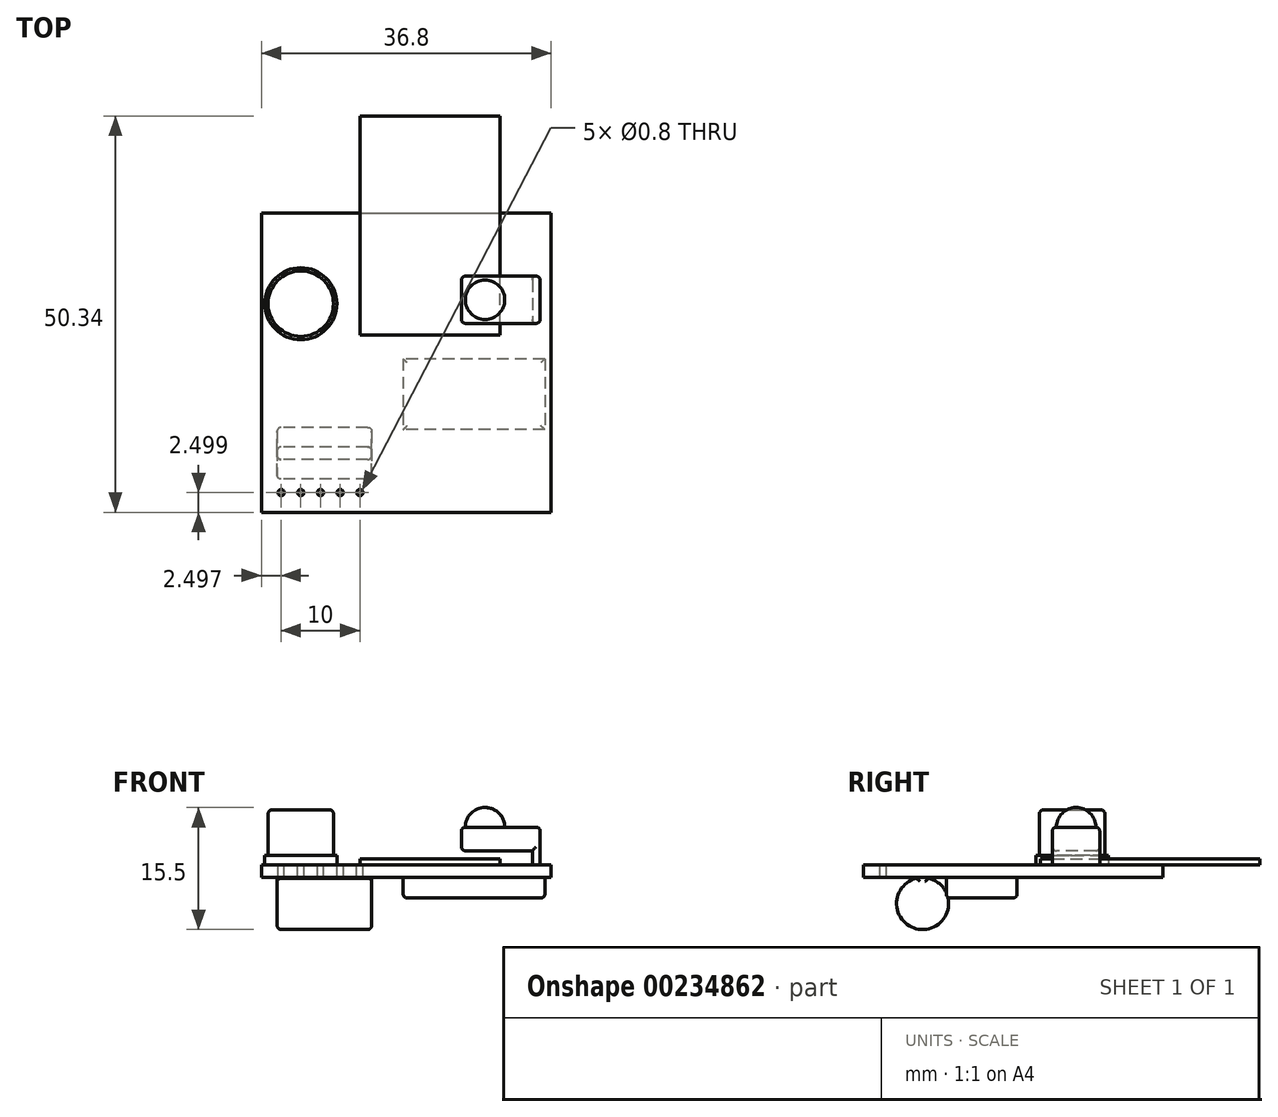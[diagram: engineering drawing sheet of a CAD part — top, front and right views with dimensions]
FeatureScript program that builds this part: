
annotation { "Feature Type Name" : "Feature", "Feature Type Description" : "" }
export const myFeature = defineFeature(function(context is Context, id is Id, definition is map)
    precondition{}
    {
        {
            var Q0;
            Q0=qCreatedBy(makeId("Top.planeOp"),FACE);
            var sketch = newSketch(context, id + "F0", { "sketchPlane" : qUnion([Q0])});
            skCircle(sketch, "E0", {"center": v(-33.02, 18.3) * mm, "radius": 4.15 * mm});
            skLineSegment(sketch, "E1.bottom", {"start": v(-38.02, 29.8) * mm, "end": v(-1.22, 29.8) * mm});
            skLineSegment(sketch, "E1.top", {"start": v(-38.02, -8.2) * mm, "end": v(-1.22, -8.2) * mm});
            skLineSegment(sketch, "E1.left", {"start": v(-38.02, 29.8) * mm, "end": v(-38.02, -8.2) * mm});
            skLineSegment(sketch, "E1.right", {"start": v(-1.22, 29.8) * mm, "end": v(-1.22, -8.2) * mm});
            skLineSegment(sketch, "E2", {"start": v(-33.02, 18.3) * mm, "end": v(-38.02, 18.3) * mm, "construction": true});
            skLineSegment(sketch, "E3", {"start": v(-33.02, 18.3) * mm, "end": v(-33.02, 29.8) * mm, "construction": true});
            skLineSegment(sketch, "E4", {"start": v(-7.72, 29.8) * mm, "end": v(-7.72, 42.15) * mm});
            skLineSegment(sketch, "E5", {"start": v(-7.72, 42.15) * mm, "end": v(-25.52, 42.15) * mm});
            skLineSegment(sketch, "E6", {"start": v(-25.52, 42.15) * mm, "end": v(-25.52, 29.8) * mm});
            skLineSegment(sketch, "E7", {"start": v(-2.62, 21.8) * mm, "end": v(-12.62, 21.8) * mm});
            skLineSegment(sketch, "E8", {"start": v(-12.62, 21.8) * mm, "end": v(-12.62, 15.8) * mm});
            skLineSegment(sketch, "E9", {"start": v(-12.62, 15.8) * mm, "end": v(-2.62, 15.8) * mm});
            skLineSegment(sketch, "E10", {"start": v(-2.62, 15.8) * mm, "end": v(-2.62, 21.8) * mm});
            skSolve(sketch);
        }
        {
            var Q0;
            Q0=makeQuery(id+"F0.imprint","IMPRINT",FACE,{"disambiguationData":[TD([[makeQuery(id+"F0.imprint","IMPRINT",EDGE,{"derivedFrom":sQuery(id+"F0.wireOp",EDGE,"E0")}),-1.0]])]});
            var Q1;
            Q1=makeQuery(id+"F0.imprint","IMPRINT",FACE,{"disambiguationData":[TD([[makeQuery(id+"F0.imprint","IMPRINT",EDGE,{"derivedFrom":sQuery(id+"F0.wireOp",EDGE,"E0")}),1.0]])]});
            var Q2;
            Q2=makeQuery(id+"F0.imprint","IMPRINT",FACE,{"disambiguationData":[TD([[makeQuery(id+"F0.imprint","IMPRINT",EDGE,{"derivedFrom":sQuery(id+"F0.wireOp",EDGE,"E7")}),1.0]])]});
            extrude(context, id + "F1", {"entities" : qUnion([Q0, Q1, Q2]), "oppositeDirection" : true, "depth" : 1.6 * mm});
        }
        {
            var Q0;
            Q0=makeQuery(id+"F0.imprint","IMPRINT",FACE,{"disambiguationData":[TD([[makeQuery(id+"F0.imprint","IMPRINT",EDGE,{"derivedFrom":sQuery(id+"F0.wireOp",EDGE,"E0")}),-1.0]])]});
            var sketch = newSketch(context, id + "F2", { "sketchPlane" : qUnion([Q0])});
            skCircle(sketch, "E11.0", {"center": v(-33.02, 18.3) * mm, "radius": 4.15 * mm});
            skLineSegment(sketch, "E12.0.0", {"start": v(-12.62, 15.8) * mm, "end": v(-2.62, 15.8) * mm});
            skLineSegment(sketch, "E12.0.1", {"start": v(-2.62, 15.8) * mm, "end": v(-2.62, 21.8) * mm});
            skLineSegment(sketch, "E12.0.2", {"start": v(-2.62, 21.8) * mm, "end": v(-12.62, 21.8) * mm});
            skLineSegment(sketch, "E12.0.3", {"start": v(-12.62, 21.8) * mm, "end": v(-12.62, 15.8) * mm});
            skLineSegment(sketch, "E13.0.0", {"start": v(-7.72, 42.15) * mm, "end": v(-25.52, 42.15) * mm});
            skLineSegment(sketch, "E13.0.1", {"start": v(-25.52, 42.15) * mm, "end": v(-25.52, 29.8) * mm});
            skLineSegment(sketch, "E13.0.2", {"start": v(-25.52, 29.8) * mm, "end": v(-7.72, 29.8) * mm});
            skLineSegment(sketch, "E13.0.3", {"start": v(-7.72, 29.8) * mm, "end": v(-7.72, 42.15) * mm});
            skLineSegment(sketch, "E14", {"start": v(-25.52, 29.8) * mm, "end": v(-25.52, 14.3) * mm});
            skLineSegment(sketch, "E15", {"start": v(-25.52, 14.3) * mm, "end": v(-7.72, 14.3) * mm});
            skLineSegment(sketch, "E16", {"start": v(-7.72, 14.3) * mm, "end": v(-7.72, 29.8) * mm});
            skCircle(sketch, "E17", {"center": v(-33.02, 18.3) * mm, "radius": 4.58 * mm});
            skSolve(sketch);
        }
        {
            var Q0;
            Q0=makeQuery(id+"F2.imprint","IMPRINT",FACE,{"disambiguationData":[TD([[makeQuery(id+"F2.imprint","IMPRINT",EDGE,{"derivedFrom":sQuery(id+"F2.wireOp",EDGE,"E11.0")}),-1.0]])]});
            var Q1;
            Q1=makeQuery(id+"F2.imprint","IMPRINT",FACE,{"disambiguationData":[TD([[makeQuery(id+"F2.imprint","IMPRINT",EDGE,{"derivedFrom":sQuery(id+"F2.wireOp",EDGE,"E11.0")}),1.0]])]});
            extrude(context, id + "F3", {"entities" : qUnion([Q0, Q1]), "operationType" : NewBodyOperationType.ADD, "depth" : 1.2 * mm});
        }
        {
            var Q0;
            Q0=makeQuery(id+"F3.opExtrude","CAP_FACE",FACE,{"disambiguationData":[OSD([sQuery(id+"F2.wireOp",EDGE,"E17")])],"isStart":false});
            var sketch = newSketch(context, id + "F4", { "sketchPlane" : qUnion([Q0])});
            skCircle(sketch, "E18.0", {"center": v(-33.02, 18.3) * mm, "radius": 4.15 * mm});
            skSolve(sketch);
        }
        {
            var Q0;
            Q0=makeQuery(id+"F4.imprint","IMPRINT",FACE,{"disambiguationData":[TD([[makeQuery(id+"F4.imprint","IMPRINT",EDGE,{"derivedFrom":sQuery(id+"F4.wireOp",EDGE,"E18.0")}),1.0]])]});
            extrude(context, id + "F5", {"entities" : qUnion([Q0]), "operationType" : NewBodyOperationType.ADD, "depth" : 5.8 * mm});
        }
        {
            var Q0;
            {var subQ0=sQuery(id+"F2.wireOp",EDGE,"E12.0.3");Q0=makeQuery(id+"F2.imprint","IMPRINT",FACE,{"disambiguationData":[TD([[makeQuery(id+"F2.imprint","IMPRINT",EDGE,{"derivedFrom":subQ0}),1.0]])]});}
            var Q1;
            {var subQ0=sQuery(id+"F2.wireOp",EDGE,"E12.0.3");Q1=makeQuery(id+"F2.imprint","IMPRINT",FACE,{"disambiguationData":[TD([[makeQuery(id+"F2.imprint","IMPRINT",EDGE,{"derivedFrom":subQ0}),-1.0]])]});}
            var Q2;
            Q2=makeQuery(id+"F2.imprint","IMPRINT",FACE,{"disambiguationData":[TD([[makeQuery(id+"F2.imprint","IMPRINT",EDGE,{"derivedFrom":sQuery(id+"F2.wireOp",EDGE,"E13.0.0")}),1.0]])]});
            extrude(context, id + "F6", {"entities" : qUnion([Q0, Q1, Q2]), "operationType" : NewBodyOperationType.ADD, "depth" : 0.8 * mm});
        }
        {
            var Q0;
            Q0=makeQuery(id+"F6.opExtrude","CAP_FACE",FACE,{"disambiguationData":[OSD([sQuery(id+"F2.wireOp",EDGE,"E13.0.0"),sQuery(id+"F2.wireOp",EDGE,"E13.0.1"),sQuery(id+"F2.wireOp",EDGE,"E13.0.3"),sQuery(id+"F2.wireOp",EDGE,"E14"),sQuery(id+"F2.wireOp",EDGE,"E15"),sQuery(id+"F2.wireOp",EDGE,"E16")])],"isStart":false});
            cPlane(context, id + "F7", {"entities" : qUnion([Q0]), "cplaneType" : CPlaneType.OFFSET, "offset" : 1 * mm, "width" : 150 * mm, "height" : 150 * mm});
        }
        {
            var Q0;
            Q0=qCreatedBy(id+"F7.planeOp",FACE);
            var sketch = newSketch(context, id + "F8", { "sketchPlane" : qUnion([Q0])});
            skLineSegment(sketch, "E19.0", {"start": v(-2.62, 21.8) * mm, "end": v(-12.62, 21.8) * mm});
            skLineSegment(sketch, "E20.0", {"start": v(-2.62, 15.8) * mm, "end": v(-2.62, 21.8) * mm});
            skLineSegment(sketch, "E21.0", {"start": v(-12.62, 15.8) * mm, "end": v(-2.62, 15.8) * mm});
            skLineSegment(sketch, "E22.0", {"start": v(-12.62, 21.8) * mm, "end": v(-12.62, 15.8) * mm});
            skSolve(sketch);
        }
        {
            var Q0;
            {var subQ10=sQuery(id+"F2.wireOp",EDGE,"E12.0.1");Q0=makeQuery(id+"F2.imprint","IMPRINT",FACE,{"disambiguationData":[TD([[makeQuery(id+"F2.imprint","IMPRINT",EDGE,{"derivedFrom":subQ10}),-1.0]])]});}
            var sketch = newSketch(context, id + "F9", { "sketchPlane" : qUnion([Q0])});
            skLineSegment(sketch, "E23", {"start": v(-3.62, 21.8) * mm, "end": v(-3.62, 15.8) * mm});
            skLineSegment(sketch, "E24", {"start": v(-3.62, 15.8) * mm, "end": v(-2.62, 15.8) * mm});
            skLineSegment(sketch, "E25", {"start": v(-2.62, 15.8) * mm, "end": v(-2.62, 21.8) * mm});
            skLineSegment(sketch, "E26", {"start": v(-2.62, 21.8) * mm, "end": v(-3.62, 21.8) * mm});
            skSolve(sketch);
        }
        {
            var Q0;
            Q0=makeQuery(id+"F9.imprint","IMPRINT",FACE,{"disambiguationData":[TD([[makeQuery(id+"F9.imprint","IMPRINT",EDGE,{"derivedFrom":sQuery(id+"F9.wireOp",EDGE,"E23")}),1.0]])]});
            extrude(context, id + "F10", {"entities" : qUnion([Q0]), "operationType" : NewBodyOperationType.ADD, "depth" : 1.8 * mm});
        }
        {
            var Q0;
            Q0=makeQuery(id+"F8.imprint","IMPRINT",FACE,{"disambiguationData":[TD([[makeQuery(id+"F8.imprint","IMPRINT",EDGE,{"derivedFrom":sQuery(id+"F8.wireOp",EDGE,"E19.0")}),1.0]])]});
            extrude(context, id + "F11", {"entities" : qUnion([Q0]), "operationType" : NewBodyOperationType.ADD, "depth" : 3 * mm});
        }
        {
            var Q0;
            Q0=makeQuery(id+"F11.opExtrude","CAP_FACE",FACE,{"disambiguationData":[OSD([sQuery(id+"F8.wireOp",EDGE,"E19.0"),sQuery(id+"F8.wireOp",EDGE,"E20.0"),sQuery(id+"F8.wireOp",EDGE,"E21.0"),sQuery(id+"F8.wireOp",EDGE,"E22.0")])],"isStart":false});
            var sketch = newSketch(context, id + "F12", { "sketchPlane" : qUnion([Q0])});
            skCircle(sketch, "E27", {"center": v(-9.62, 18.8) * mm, "radius": 2.5 * mm});
            skSolve(sketch);
        }
        {
            var Q0;
            Q0=makeQuery(id+"F12.imprint","IMPRINT",FACE,{"disambiguationData":[TD([[makeQuery(id+"F12.imprint","IMPRINT",EDGE,{"derivedFrom":sQuery(id+"F12.wireOp",EDGE,"E27")}),1.0]])]});
            extrude(context, id + "F13", {"entities" : qUnion([Q0]), "operationType" : NewBodyOperationType.ADD, "depth" : 2.5 * mm});
        }
        {
            var Q0;
            Q0=makeQuery(id+"F13.opExtrude","CAP_EDGE",EDGE,{"disambiguationData":[OSD([sQuery(id+"F12.wireOp",EDGE,"E27")])],"isStart":false});
            fillet(context, id + "F14", {"entities" : qUnion([Q0]), "radius" : 2.5 * mm, "tangentPropagation" : true, "allowEdgeOverflow" : false});
        }
        {
            var Q0;
            Q0=makeQuery(id+"F11.opExtrude","CAP_EDGE",EDGE,{"disambiguationData":[OSD([sQuery(id+"F8.wireOp",EDGE,"E21.0")])],"isStart":false});
            var Q1;
            Q1=makeQuery(id+"F11.opExtrude","CAP_EDGE",EDGE,{"disambiguationData":[OSD([sQuery(id+"F8.wireOp",EDGE,"E19.0")])],"isStart":false});
            var Q2;
            Q2=makeQuery(id+"F11.opExtrude","CAP_EDGE",EDGE,{"disambiguationData":[OSD([sQuery(id+"F8.wireOp",EDGE,"E20.0")])],"isStart":false});
            var Q3;
            Q3=makeQuery(id+"F11.boolean.opBoolean","MERGE",EDGE,{"derivedFrom":[makeQuery(id+"F10.opExtrude","SWEPT_EDGE",EDGE,{"disambiguationData":[OSD([sQuery(id+"F9.wireOp",EDGE,"E24"),sQuery(id+"F9.wireOp",EDGE,"E25")])]}),makeQuery(id+"F11.opExtrude","SWEPT_EDGE",EDGE,{"disambiguationData":[OSD([sQuery(id+"F8.wireOp",EDGE,"E20.0"),sQuery(id+"F8.wireOp",EDGE,"E21.0")])]})]});
            var Q4;
            Q4=makeQuery(id+"F11.boolean.opBoolean","MERGE",EDGE,{"derivedFrom":[makeQuery(id+"F10.opExtrude","SWEPT_EDGE",EDGE,{"disambiguationData":[OSD([sQuery(id+"F9.wireOp",EDGE,"E25"),sQuery(id+"F9.wireOp",EDGE,"E26")])]}),makeQuery(id+"F11.opExtrude","SWEPT_EDGE",EDGE,{"disambiguationData":[OSD([sQuery(id+"F8.wireOp",EDGE,"E19.0"),sQuery(id+"F8.wireOp",EDGE,"E20.0")])]})]});
            var Q5;
            Q5=makeQuery(id+"F10.opExtrude","SWEPT_EDGE",EDGE,{"disambiguationData":[OSD([sQuery(id+"F2.wireOp",EDGE,"E12.0.0"),sQuery(id+"F9.wireOp",EDGE,"E23"),sQuery(id+"F9.wireOp",EDGE,"E24")])]});
            var Q6;
            Q6=makeQuery(id+"F11.opExtrude","CAP_EDGE",EDGE,{"disambiguationData":[OSD([sQuery(id+"F8.wireOp",EDGE,"E21.0")])],"isStart":true});
            var Q7;
            Q7=makeQuery(id+"F11.opExtrude","SWEPT_FACE",FACE,{"disambiguationData":[OSD([sQuery(id+"F8.wireOp",EDGE,"E22.0")])]});
            var Q8;
            Q8=makeQuery(id+"F11.opExtrude","CAP_EDGE",EDGE,{"disambiguationData":[OSD([sQuery(id+"F8.wireOp",EDGE,"E19.0")])],"isStart":true});
            var Q9;
            Q9=makeQuery(id+"F10.opExtrude","SWEPT_EDGE",EDGE,{"disambiguationData":[OSD([sQuery(id+"F2.wireOp",EDGE,"E12.0.2"),sQuery(id+"F9.wireOp",EDGE,"E23"),sQuery(id+"F9.wireOp",EDGE,"E26")])]});
            var Q10;
            Q10=makeQuery(id+"F5.opExtrude","CAP_FACE",FACE,{"disambiguationData":[OSD([sQuery(id+"F4.wireOp",EDGE,"E18.0")])],"isStart":false});
            fillet(context, id + "F15", {"entities" : qUnion([Q0, Q1, Q2, Q3, Q4, Q5, Q6, Q7, Q8, Q9, Q10]), "radius" : 0.5 * mm, "tangentPropagation" : true, "allowEdgeOverflow" : false});
        }
        {
            var Q0;
            Q0=makeQuery(id+"F1.opExtrude","CAP_FACE",FACE,{"disambiguationData":[OSD([sQuery(id+"F0.wireOp",EDGE,"E1.bottom"),sQuery(id+"F0.wireOp",EDGE,"E1.top"),sQuery(id+"F0.wireOp",EDGE,"E1.left"),sQuery(id+"F0.wireOp",EDGE,"E1.right")])],"isStart":true});
            var sketch = newSketch(context, id + "F16", { "sketchPlane" : qUnion([Q0])});
            skCircle(sketch, "E28", {"center": v(-35.52, -5.7) * mm, "radius": 0.4 * mm});
            skCircle(sketch, "E29", {"center": v(-33.02, -5.7) * mm, "radius": 0.4 * mm});
            skCircle(sketch, "E30", {"center": v(-30.52, -5.7) * mm, "radius": 0.4 * mm});
            skCircle(sketch, "E31", {"center": v(-28.02, -5.7) * mm, "radius": 0.4 * mm});
            skCircle(sketch, "E32", {"center": v(-25.52, -5.7) * mm, "radius": 0.4 * mm});
            skSolve(sketch);
        }
        {
            var Q0;
            Q0=makeQuery(id+"F16.imprint","IMPRINT",FACE,{"disambiguationData":[TD([[makeQuery(id+"F16.imprint","IMPRINT",EDGE,{"derivedFrom":sQuery(id+"F16.wireOp",EDGE,"E28")}),1.0]])]});
            var Q1;
            Q1=makeQuery(id+"F16.imprint","IMPRINT",FACE,{"disambiguationData":[TD([[makeQuery(id+"F16.imprint","IMPRINT",EDGE,{"derivedFrom":sQuery(id+"F16.wireOp",EDGE,"E29")}),1.0]])]});
            var Q2;
            Q2=makeQuery(id+"F16.imprint","IMPRINT",FACE,{"disambiguationData":[TD([[makeQuery(id+"F16.imprint","IMPRINT",EDGE,{"derivedFrom":sQuery(id+"F16.wireOp",EDGE,"E30")}),1.0]])]});
            var Q3;
            Q3=makeQuery(id+"F16.imprint","IMPRINT",FACE,{"disambiguationData":[TD([[makeQuery(id+"F16.imprint","IMPRINT",EDGE,{"derivedFrom":sQuery(id+"F16.wireOp",EDGE,"E31")}),1.0]])]});
            var Q4;
            Q4=makeQuery(id+"F16.imprint","IMPRINT",FACE,{"disambiguationData":[TD([[makeQuery(id+"F16.imprint","IMPRINT",EDGE,{"derivedFrom":sQuery(id+"F16.wireOp",EDGE,"E32")}),1.0]])]});
            extrude(context, id + "F17", {"entities" : qUnion([Q0, Q1, Q2, Q3, Q4]), "operationType" : NewBodyOperationType.REMOVE, "oppositeDirection" : true, "depth" : 25 * mm});
        }
        {
            var Q0;
            Q0=makeQuery(id+"F1.opExtrude","SWEPT_FACE",FACE,{"disambiguationData":[OSD([sQuery(id+"F0.wireOp",EDGE,"E1.left")])]});
            cPlane(context, id + "F18", {"entities" : qUnion([Q0]), "cplaneType" : CPlaneType.OFFSET, "offset" : 2 * mm, "oppositeDirection" : true, "width" : 150 * mm, "height" : 150 * mm});
        }
        {
            var Q0;
            Q0=qCreatedBy(id+"F18.planeOp",FACE);
            var sketch = newSketch(context, id + "F19", { "sketchPlane" : qUnion([Q0])});
            skCircle(sketch, "E33", {"center": v(0.7, -4.9) * mm, "radius": 3.3 * mm});
            skLineSegment(sketch, "E34", {"start": v(8.2, -1.6) * mm, "end": v(0.7, -1.6) * mm, "construction": true});
            skLineSegment(sketch, "E35.0", {"start": v(-29.8, -1.6) * mm, "end": v(8.2, -1.6) * mm, "construction": true});
            skLineSegment(sketch, "E36", {"start": v(1.5, -1.6) * mm, "end": v(1.5, -1.7) * mm});
            skLineSegment(sketch, "E37", {"start": v(-0.11, -1.6) * mm, "end": v(-0.11, -1.7) * mm});
            skLineSegment(sketch, "E38", {"start": v(1.5, -1.6) * mm, "end": v(-0.11, -1.6) * mm});
            skSolve(sketch);
        }
        {
            var Q0;
            Q0=makeQuery(id+"F19.imprint","IMPRINT",FACE,{"disambiguationData":[TD([[makeQuery(id+"F19.imprint","IMPRINT",EDGE,{"derivedFrom":sQuery(id+"F19.wireOp",EDGE,"E33")}),1.0]])]});
            var Q1;
            {var subQ0=sQuery(id+"F19.wireOp",EDGE,"E36");Q1=makeQuery(id+"F19.imprint","IMPRINT",FACE,{"disambiguationData":[TD([[makeQuery(id+"F19.imprint","IMPRINT",EDGE,{"derivedFrom":subQ0}),-1.0]])]});}
            var Q2;
            {var subQ0=sQuery(id+"F19.wireOp",EDGE,"E37");Q2=makeQuery(id+"F19.imprint","IMPRINT",FACE,{"disambiguationData":[TD([[makeQuery(id+"F19.imprint","IMPRINT",EDGE,{"derivedFrom":subQ0}),1.0]])]});}
            extrude(context, id + "F20", {"entities" : qUnion([Q0, Q1, Q2]), "operationType" : NewBodyOperationType.ADD, "oppositeDirection" : true, "depth" : 12 * mm});
        }
        {
            var Q0;
            Q0=makeQuery(id+"F20.opExtrude","CAP_EDGE",EDGE,{"disambiguationData":[OSD([sQuery(id+"F19.wireOp",EDGE,"E33")])],"isStart":true});
            var Q1;
            Q1=makeQuery(id+"F20.opExtrude","CAP_EDGE",EDGE,{"disambiguationData":[OSD([sQuery(id+"F19.wireOp",EDGE,"E37")])],"isStart":true});
            var Q2;
            Q2=makeQuery(id+"F20.opExtrude","CAP_EDGE",EDGE,{"disambiguationData":[OSD([sQuery(id+"F19.wireOp",EDGE,"E36")])],"isStart":true});
            var Q3;
            Q3=makeQuery(id+"F20.opExtrude","CAP_EDGE",EDGE,{"disambiguationData":[OSD([sQuery(id+"F19.wireOp",EDGE,"E36")])],"isStart":false});
            var Q4;
            Q4=makeQuery(id+"F20.opExtrude","CAP_EDGE",EDGE,{"disambiguationData":[OSD([sQuery(id+"F19.wireOp",EDGE,"E37")])],"isStart":false});
            var Q5;
            Q5=makeQuery(id+"F20.opExtrude","CAP_EDGE",EDGE,{"disambiguationData":[OSD([sQuery(id+"F19.wireOp",EDGE,"E33")])],"isStart":false});
            fillet(context, id + "F21", {"entities" : qUnion([Q0, Q1, Q2, Q3, Q4, Q5]), "radius" : 0.5 * mm, "tangentPropagation" : true, "allowEdgeOverflow" : false});
        }
        {
            var Q0;
            Q0=makeQuery(id+"F1.opExtrude","CAP_FACE",FACE,{"disambiguationData":[OSD([sQuery(id+"F0.wireOp",EDGE,"E1.bottom"),sQuery(id+"F0.wireOp",EDGE,"E1.top"),sQuery(id+"F0.wireOp",EDGE,"E1.left"),sQuery(id+"F0.wireOp",EDGE,"E1.right")])],"isStart":false});
            var sketch = newSketch(context, id + "F22", { "sketchPlane" : qUnion([Q0])});
            skLineSegment(sketch, "E39.bottom", {"start": v(-2.02, -11.3) * mm, "end": v(-20.02, -11.3) * mm});
            skLineSegment(sketch, "E39.top", {"start": v(-2.02, -2.3) * mm, "end": v(-20.02, -2.3) * mm});
            skLineSegment(sketch, "E39.left", {"start": v(-2.02, -11.3) * mm, "end": v(-2.02, -2.3) * mm});
            skLineSegment(sketch, "E39.right", {"start": v(-20.02, -11.3) * mm, "end": v(-20.02, -2.3) * mm});
            skLineSegment(sketch, "E40", {"start": v(-2.02, -6.8) * mm, "end": v(-2.02, 8.2) * mm, "construction": true});
            skSolve(sketch);
        }
        {
            var Q0;
            Q0=makeQuery(id+"F22.imprint","IMPRINT",FACE,{"disambiguationData":[TD([[makeQuery(id+"F22.imprint","IMPRINT",EDGE,{"derivedFrom":sQuery(id+"F22.wireOp",EDGE,"E39.bottom")}),-1.0]])]});
            extrude(context, id + "F23", {"entities" : qUnion([Q0]), "operationType" : NewBodyOperationType.ADD, "depth" : 2.6 * mm});
        }
        {
            var Q0;
            Q0=makeQuery(id+"F23.opExtrude","CAP_EDGE",EDGE,{"disambiguationData":[OSD([sQuery(id+"F22.wireOp",EDGE,"E39.top")])],"isStart":false});
            var Q1;
            Q1=makeQuery(id+"F23.opExtrude","CAP_EDGE",EDGE,{"disambiguationData":[OSD([sQuery(id+"F22.wireOp",EDGE,"E39.right")])],"isStart":false});
            var Q2;
            Q2=makeQuery(id+"F23.opExtrude","CAP_EDGE",EDGE,{"disambiguationData":[OSD([sQuery(id+"F22.wireOp",EDGE,"E39.bottom")])],"isStart":false});
            var Q3;
            Q3=makeQuery(id+"F23.opExtrude","CAP_EDGE",EDGE,{"disambiguationData":[OSD([sQuery(id+"F22.wireOp",EDGE,"E39.left")])],"isStart":false});
            fillet(context, id + "F24", {"entities" : qUnion([Q0, Q1, Q2, Q3]), "radius" : 0.5 * mm, "tangentPropagation" : true, "allowEdgeOverflow" : false});
        }
    });
